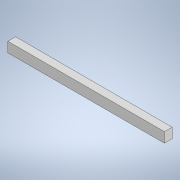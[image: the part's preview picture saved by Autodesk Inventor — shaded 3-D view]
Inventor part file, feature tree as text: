
AUTODESK INVENTOR PART (.ipt)
format: ipt  version: 2022 (Build 260153000, 153)  size: 107,008 bytes
history: native  units: in
note: dims shown in document units (in); Inventor stores cm internally (conversion verified against a paired STEP export)
features: sheet_metal_op x1, sketch x1, other x1
ambient origin geometry x8: Origin, YZ Plane, XZ Plane, XY Plane, X Axis, Y Axis, Z Axis, Center Point
bodies: Solid1 (feature_tree)
feature tree (3):
  sheet_metal_op  "Face1"
  sketch  "Sketch3"  dims[d3=1.1949in d4=0.0768in d5=0.0591in]
  other  "Plate1"
